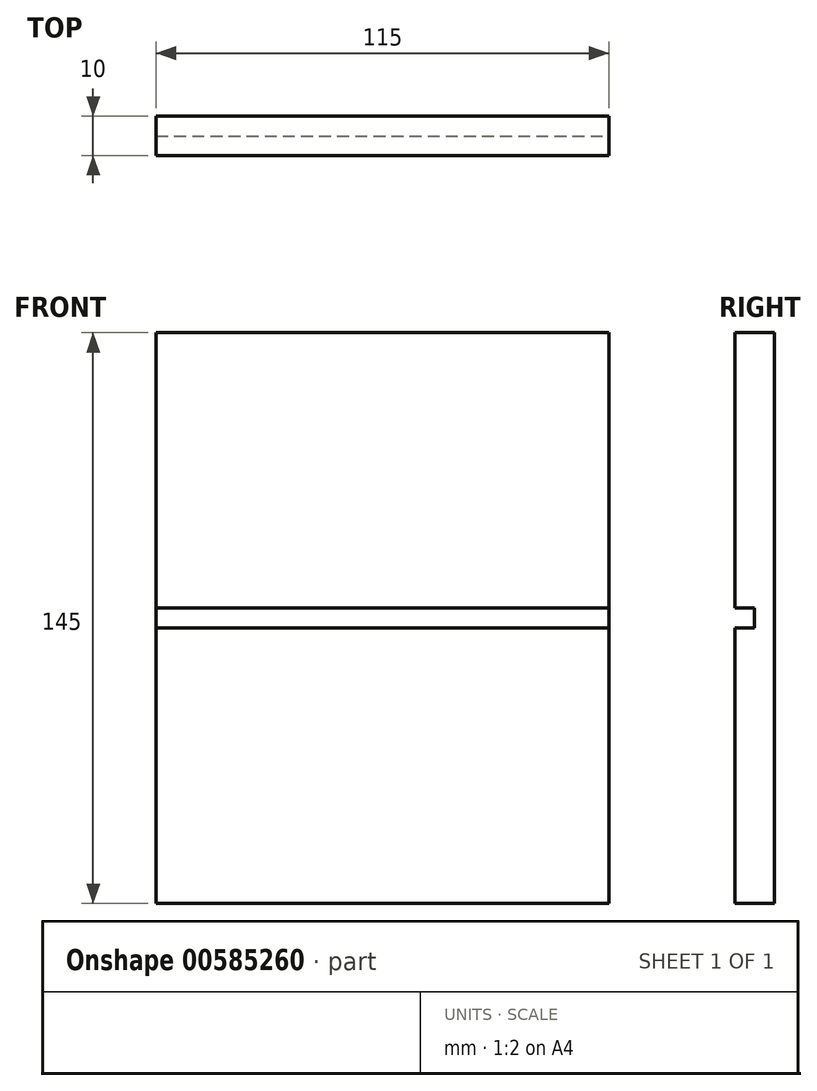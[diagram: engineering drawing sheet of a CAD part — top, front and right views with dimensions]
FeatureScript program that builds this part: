
annotation { "Feature Type Name" : "Feature", "Feature Type Description" : "" }
export const myFeature = defineFeature(function(context is Context, id is Id, definition is map)
    precondition{}
    {
        {
            var Q0;
            Q0=qCreatedBy(makeId("Front.planeOp"),FACE);
            var sketch = newSketch(context, id + "F0", { "sketchPlane" : qUnion([Q0])});
            skLineSegment(sketch, "E0.bottom", {"start": v(-2.2, 70) * mm, "end": v(-117.2, 70) * mm});
            skLineSegment(sketch, "E1", {"start": v(-117.2, 70) * mm, "end": v(-117.2, 0) * mm});
            skLineSegment(sketch, "E2", {"start": v(-2.2, 70) * mm, "end": v(-2.2, 0) * mm});
            skLineSegment(sketch, "E3", {"start": v(-117.2, 0) * mm, "end": v(-2.2, 0) * mm});
            skLineSegment(sketch, "E4", {"start": v(-117.2, 0) * mm, "end": v(-117.2, -5) * mm});
            skLineSegment(sketch, "E5", {"start": v(-117.2, -5) * mm, "end": v(-2.2, -5) * mm});
            skLineSegment(sketch, "E6", {"start": v(-2.2, 0) * mm, "end": v(-2.2, -5) * mm});
            skLineSegment(sketch, "E7", {"start": v(-2.2, -5) * mm, "end": v(-2.2, -75) * mm});
            skLineSegment(sketch, "E8", {"start": v(-117.2, -5) * mm, "end": v(-117.2, -75) * mm});
            skLineSegment(sketch, "E9", {"start": v(-117.2, -75) * mm, "end": v(-2.2, -75) * mm});
            skSolve(sketch);
        }
        {
            var Q0;
            Q0=makeQuery(id+"F0.imprint","IMPRINT",FACE,{"disambiguationData":[TD([[makeQuery(id+"F0.imprint","IMPRINT",EDGE,{"derivedFrom":sQuery(id+"F0.wireOp",EDGE,"E3")}),-1.0]])]});
            extrude(context, id + "F1", {"entities" : qUnion([Q0]), "depth" : 5 * mm, "offsetDistance" : 25 * mm});
        }
        {
            var Q0;
            Q0=makeQuery(id+"F0.imprint","IMPRINT",FACE,{"disambiguationData":[TD([[makeQuery(id+"F0.imprint","IMPRINT",EDGE,{"derivedFrom":sQuery(id+"F0.wireOp",EDGE,"E0.bottom")}),1.0]])]});
            var Q1;
            Q1=makeQuery(id+"F0.imprint","IMPRINT",FACE,{"disambiguationData":[TD([[makeQuery(id+"F0.imprint","IMPRINT",EDGE,{"derivedFrom":sQuery(id+"F0.wireOp",EDGE,"E5")}),-1.0]])]});
            extrude(context, id + "F2", {"entities" : qUnion([Q0, Q1]), "operationType" : NewBodyOperationType.ADD, "depth" : 10 * mm, "offsetDistance" : 25 * mm});
        }
    });
